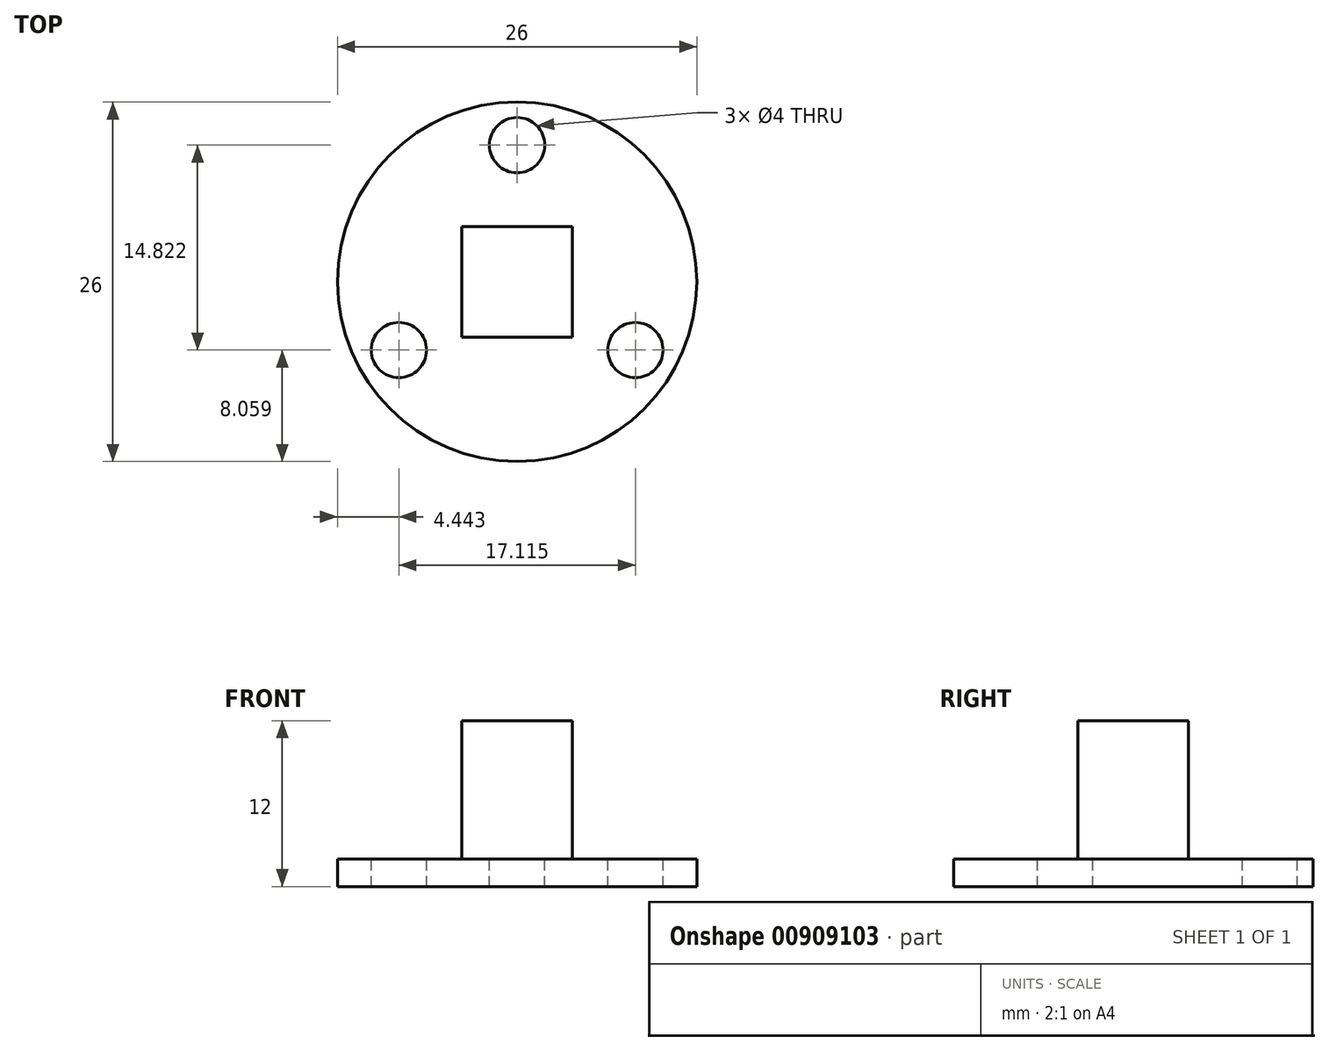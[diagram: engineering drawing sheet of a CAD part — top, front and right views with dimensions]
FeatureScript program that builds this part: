
annotation { "Feature Type Name" : "Feature", "Feature Type Description" : "" }
export const myFeature = defineFeature(function(context is Context, id is Id, definition is map)
    precondition{}
    {
        {
            var Q0;
            Q0=qCreatedBy(makeId("Top.planeOp"),FACE);
            var sketch = newSketch(context, id + "F0", { "sketchPlane" : qUnion([Q0])});
            skCircle(sketch, "E0", {"center": v(0, 0) * mm, "radius": 13 * mm});
            skSolve(sketch);
        }
        {
            var Q0;
            Q0=makeQuery(id+"F0.imprint","IMPRINT",FACE,{"disambiguationData":[TD([[makeQuery(id+"F0.imprint","IMPRINT",EDGE,{"derivedFrom":sQuery(id+"F0.wireOp",EDGE,"E0")}),1.0]])]});
            extrude(context, id + "F1", {"entities" : qUnion([Q0]), "depth" : 2 * mm, "offsetDistance" : 25 * mm});
        }
        {
            var Q0;
            Q0=makeQuery(id+"F1.opExtrude","CAP_FACE",FACE,{"disambiguationData":[OSD([sQuery(id+"F0.wireOp",EDGE,"E0")])],"isStart":false});
            var sketch = newSketch(context, id + "F2", { "sketchPlane" : qUnion([Q0])});
            skLineSegment(sketch, "E1.bottom", {"start": v(4, -4) * mm, "end": v(-4, -4) * mm});
            skLineSegment(sketch, "E1.top", {"start": v(4, 4) * mm, "end": v(-4, 4) * mm});
            skLineSegment(sketch, "E1.left", {"start": v(4, -4) * mm, "end": v(4, 4) * mm});
            skLineSegment(sketch, "E1.right", {"start": v(-4, -4) * mm, "end": v(-4, 4) * mm});
            skPoint(sketch, "E1.middle", {"position": v(0, 0) * mm});
            skSolve(sketch);
        }
        {
            var Q0;
            Q0=makeQuery(id+"F2.imprint","IMPRINT",FACE,{"disambiguationData":[TD([[makeQuery(id+"F2.imprint","IMPRINT",EDGE,{"derivedFrom":sQuery(id+"F2.wireOp",EDGE,"E1.bottom")}),-1.0]])]});
            extrude(context, id + "F3", {"entities" : qUnion([Q0]), "operationType" : NewBodyOperationType.ADD, "depth" : 10 * mm, "offsetDistance" : 25 * mm});
        }
        {
            var Q0;
            Q0=makeQuery(id+"F1.opExtrude","CAP_FACE",FACE,{"disambiguationData":[OSD([sQuery(id+"F0.wireOp",EDGE,"E0")])],"isStart":false});
            var sketch = newSketch(context, id + "F4", { "sketchPlane" : qUnion([Q0])});
            skCircle(sketch, "E2", {"center": v(0, 9.88) * mm, "radius": 2 * mm});
            skCircle(sketch, "E3.1.0", {"center": v(-8.56, -4.94) * mm, "radius": 2 * mm});
            skCircle(sketch, "E3.2.0", {"center": v(8.56, -4.94) * mm, "radius": 2 * mm});
            skPoint(sketch, "E3.center", {"position": v(0, 0) * mm});
            skSolve(sketch);
        }
        {
            var Q0;
            Q0=makeQuery(id+"F4.imprint","IMPRINT",FACE,{"disambiguationData":[TD([[makeQuery(id+"F4.imprint","IMPRINT",EDGE,{"derivedFrom":sQuery(id+"F4.wireOp",EDGE,"E2")}),1.0]])]});
            var Q1;
            Q1=makeQuery(id+"F4.imprint","IMPRINT",FACE,{"disambiguationData":[TD([[makeQuery(id+"F4.imprint","IMPRINT",EDGE,{"derivedFrom":sQuery(id+"F4.wireOp",EDGE,"E3.2.0")}),1.0]])]});
            var Q2;
            Q2=makeQuery(id+"F4.imprint","IMPRINT",FACE,{"disambiguationData":[TD([[makeQuery(id+"F4.imprint","IMPRINT",EDGE,{"derivedFrom":sQuery(id+"F4.wireOp",EDGE,"E3.1.0")}),1.0]])]});
            extrude(context, id + "F5", {"entities" : qUnion([Q0, Q1, Q2]), "operationType" : NewBodyOperationType.REMOVE, "oppositeDirection" : true, "depth" : 25 * mm, "offsetDistance" : 25 * mm});
        }
    });
